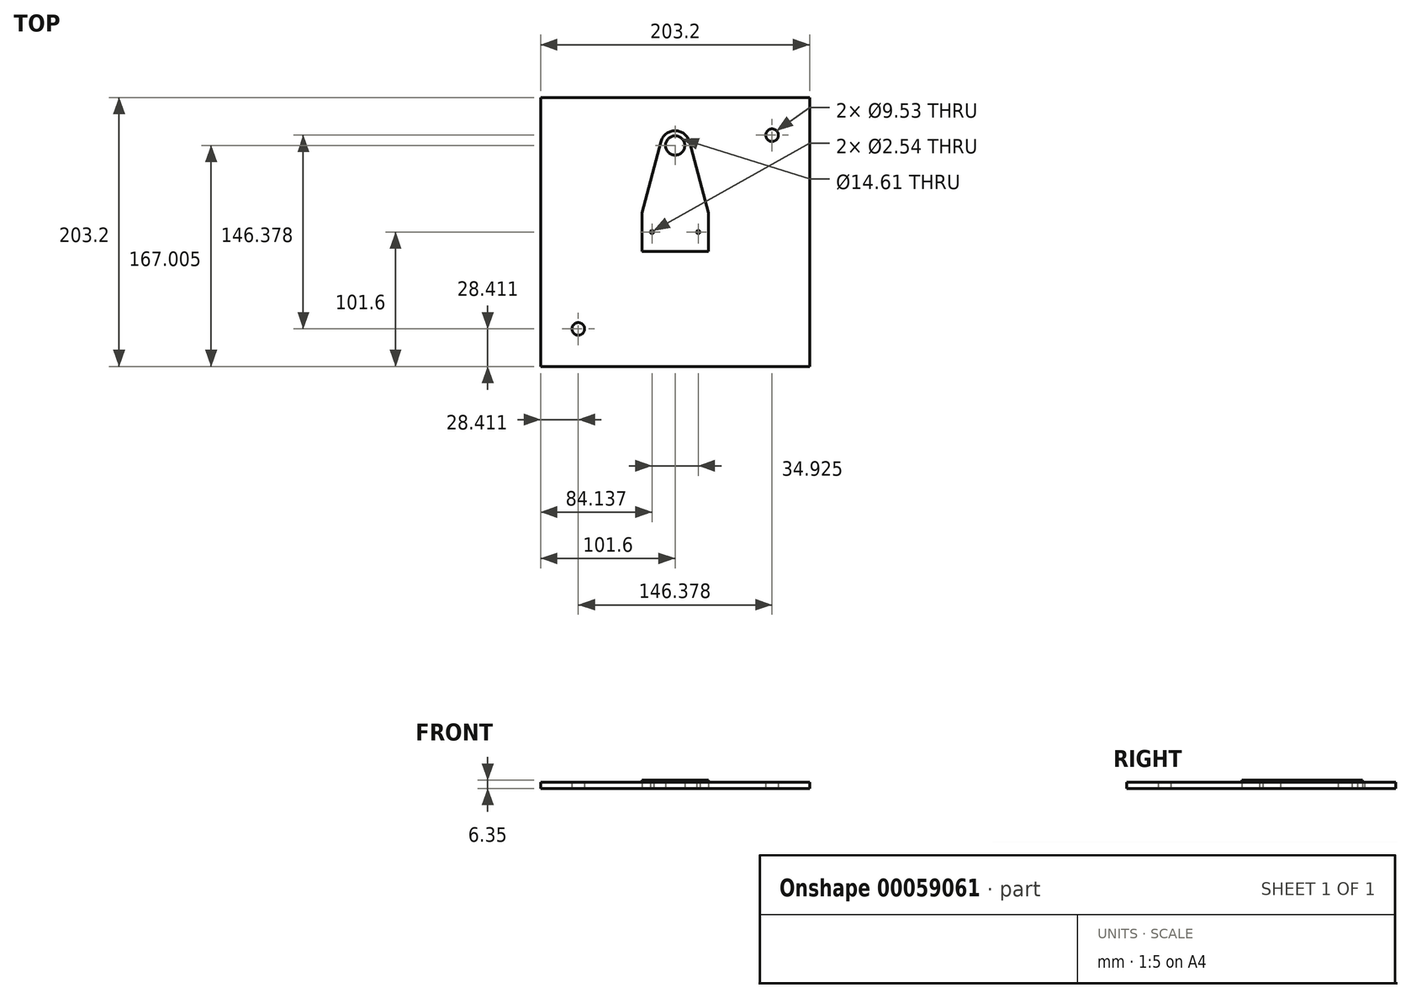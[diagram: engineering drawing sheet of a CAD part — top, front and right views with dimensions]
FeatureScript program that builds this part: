
annotation { "Feature Type Name" : "Feature", "Feature Type Description" : "" }
export const myFeature = defineFeature(function(context is Context, id is Id, definition is map)
    precondition{}
    {
        {
            var Q0;
            Q0=qCreatedBy(makeId("Top.planeOp"),FACE);
            var sketch = newSketch(context, id + "F0", { "sketchPlane" : qUnion([Q0])});
            skLineSegment(sketch, "E0.bottom", {"start": v(25.08, -14.6) * mm, "end": v(-25.08, -14.6) * mm});
            skLineSegment(sketch, "E0.top", {"start": v(25.08, 14.6) * mm, "end": v(-25.08, 14.6) * mm});
            skLineSegment(sketch, "E0.left", {"start": v(25.08, -14.6) * mm, "end": v(25.08, 14.6) * mm});
            skLineSegment(sketch, "E0.right", {"start": v(-25.08, -14.6) * mm, "end": v(-25.08, 14.6) * mm});
            skPoint(sketch, "E0.middle", {"position": v(0, 0) * mm});
            skLineSegment(sketch, "E1", {"start": v(-25.08, 14.6) * mm, "end": v(-10.74, 68.27) * mm});
            skCircle(sketch, "E2", {"center": v(0, 65.4) * mm, "radius": 4.76 * mm, "construction": true});
            skCircle(sketch, "E3.0", {"center": v(0, 65.4) * mm, "radius": 11.11 * mm});
            skCircle(sketch, "E4", {"center": v(-17.46, 0) * mm, "radius": 1.27 * mm});
            skCircle(sketch, "E5.MirrorC", {"center": v(17.46, 0) * mm, "radius": 1.27 * mm});
            skLineSegment(sketch, "E6.MirrorCS", {"start": v(25.08, 14.6) * mm, "end": v(10.74, 68.27) * mm});
            skCircle(sketch, "E7.0", {"center": v(0, 65.4) * mm, "radius": 7.3 * mm});
            skSolve(sketch);
        }
        {
            var Q0;
            Q0 = qSketchRegion(id + "F0", true);
            extrude(context, id + "F1", {"entities" : qUnion([Q0]), "depth" : 6.35 * mm});
        }
        {
            var Q0;
            Q0=qCreatedBy(makeId("Top.planeOp"),FACE);
            var sketch = newSketch(context, id + "F2", { "sketchPlane" : qUnion([Q0])});
            skLineSegment(sketch, "E8.bottom", {"start": v(101.6, -101.6) * mm, "end": v(-101.6, -101.6) * mm});
            skLineSegment(sketch, "E8.top", {"start": v(101.6, 101.6) * mm, "end": v(-101.6, 101.6) * mm});
            skLineSegment(sketch, "E8.left", {"start": v(101.6, -101.6) * mm, "end": v(101.6, 101.6) * mm});
            skLineSegment(sketch, "E8.right", {"start": v(-101.6, -101.6) * mm, "end": v(-101.6, 101.6) * mm});
            skPoint(sketch, "E8.middle", {"position": v(0, 0) * mm});
            skCircle(sketch, "E9", {"center": v(73.19, 73.19) * mm, "radius": 4.76 * mm});
            skLineSegment(sketch, "E10", {"start": v(-101.6, 101.6) * mm, "end": v(101.6, -101.6) * mm, "construction": true});
            skLineSegment(sketch, "E11", {"start": v(0, 0) * mm, "end": v(73.19, 73.19) * mm, "construction": true});
            skCircle(sketch, "E12.MirrorC", {"center": v(-73.19, -73.19) * mm, "radius": 4.76 * mm});
            skSolve(sketch);
        }
        {
            var Q0;
            Q0 = qSketchRegion(id + "F2", true);
            extrude(context, id + "F3", {"entities" : qUnion([Q0]), "depth" : 4.76 * mm});
        }
    });
